# Revit family: Lighting-ArredoUrbano-GEWISS-ELIA-BL-LED_PALO_500mm
name_source: partatom
category: Apparecchi per illuminazione
units: mm (PartAtom-declared; Revit-internal decimal feet)

## family parameters
Condiviso = No
Host = Superficie
Punto di calcolo locali = Sì
Quota connettore circolare = Usa diametro
Sorgente d'illuminazione = Sì
Taglio con vuoti quando caricato = No
Tipo di parte = Normale

## types (1)
- Lighting-ArredoUrbano-GEWISS-ELIA-BL-LED_PALO_500mm
    Alimentatore = Incluso
    Angolo campo riflettore = 90.00°
    Angolo inclinazione = 90.00°
    Angolo raggio riflettore = 30.00°
    Apparecchio a ridotta temperatura superficiale = -
    Applicazione = Esterno
    Cablaggio = Con morsetto
    Caratteristiche elettriche e gestione della luce = -
    Caratteristiche ottiche e illuminotecniche = -
    Catalogo = LIGHTING
    Certificazione DIN 18032-3 = -
    Certificazioni e classificazioni = -
    Classe fotobiologica = RG0
    Classe isolamento = I
    Classificazione: = -
    Codice EAN = 8034035077395
    Codice Electrocod = 2419
    Codice digitale univoco (Datamatrix) = Attualmente non presente
    Colore = Nero
    Contesto = Illuminazione architetturale esterna
    Controllo abbagliamento e luminanza = UGR < 25
    Corpo = Alluminio pressofuso
    Descrizione = ELIA BL ST AL ON/OFF 5700K 500 MM
    Dispositivo di protezione = DM 0,5KV / CM 1KV
    Durata di vita = L80B50 (Tq25°C) = 50.000h
    Emetti da diametro cerchio = 100 mm  [stored 0.328084 ft]
    Failure rate alimentatore = F025 = 50.000h Tq 25°C
    Filtro dei colori = 16777215
    Finitura colore = -
    Fissaggio = Supporto in acciaio INOX
    Frequenza nominale (Hz) = 50/60 Hz
    Gancio di chiusura = -
    Garanzia = 5 anni
    Grado di protezione = IP65
    Gruppo ottico = -
    Guarnizioni = -
    IDF = 977d9806-efea-4076-90bb-9c59742627c5
    IDT = 58ef68ba-15dc-4c5e-a143-12ec648dbf1a
    IPEA = -
    Immagine tipo = EliaBL.jpg
    Inclinazione = -
    Indice di resa cromatica = CRI>80
    Informazioni generali = -
    Installazione e manutenzione = -
    Lugnezza massima = 74 mm  [stored 0.242782 ft]
    Lunghezza simbolo sorgente d'illuminazione = 500 mm  [stored 1.64042 ft]
    Materiali = -
    Modello = GWF2300LR857
    Norma di riferimento = -
    Ottica = Opale diffondente
    POSIZIONE = 80000
    Produttore = GEWISS S.p.A.
    Prospetto di default = 1219 mm
    Rendi la forma visibile nel rendering = No
    Resistenza agli urti = IK08
    Resistenza al filo incandescente = 750 °C
    Scheda Tecnica = https://www.gewiss.com
    Schermo = Policarbonato
    Sistema di controllo = Stand alone
    Sostituibilità gruppo ottico = Non disponibile
    Sostituibilità piastra di cablaggio = Non disponibile
    Superficie massima esposta al vento : = -
    Temperatura di esercizio = -20° +45°
    Temperatura di stoccaggio = -20° +65°
    Tensione di alimentazione = 100-240 V
    Tipo di apparecchio = Apparecchio a LED per illuminazione diffusa
    Tipo di installazione e montaggio = Terra
    Tipologia sorgente luminosa = LED - Non sostituibile
    Tolleranza cromatica = SDCM = 5
    URL = https://www.gewiss.com
    Vano di alimentazione = Integrato
    Variazione temperatura colore lampada con luminosità attenuata = <Nessuno>
    Versione file RFA = 21.4
    Versioni = Standard 500 mm
    Viti esterne = -
    larghezza lampada = 50 mm  [stored 0.164042 ft]

note: [stored X ft] marks values corroborated as IEEE doubles in the binary element streams (Revit-internal decimal feet)
